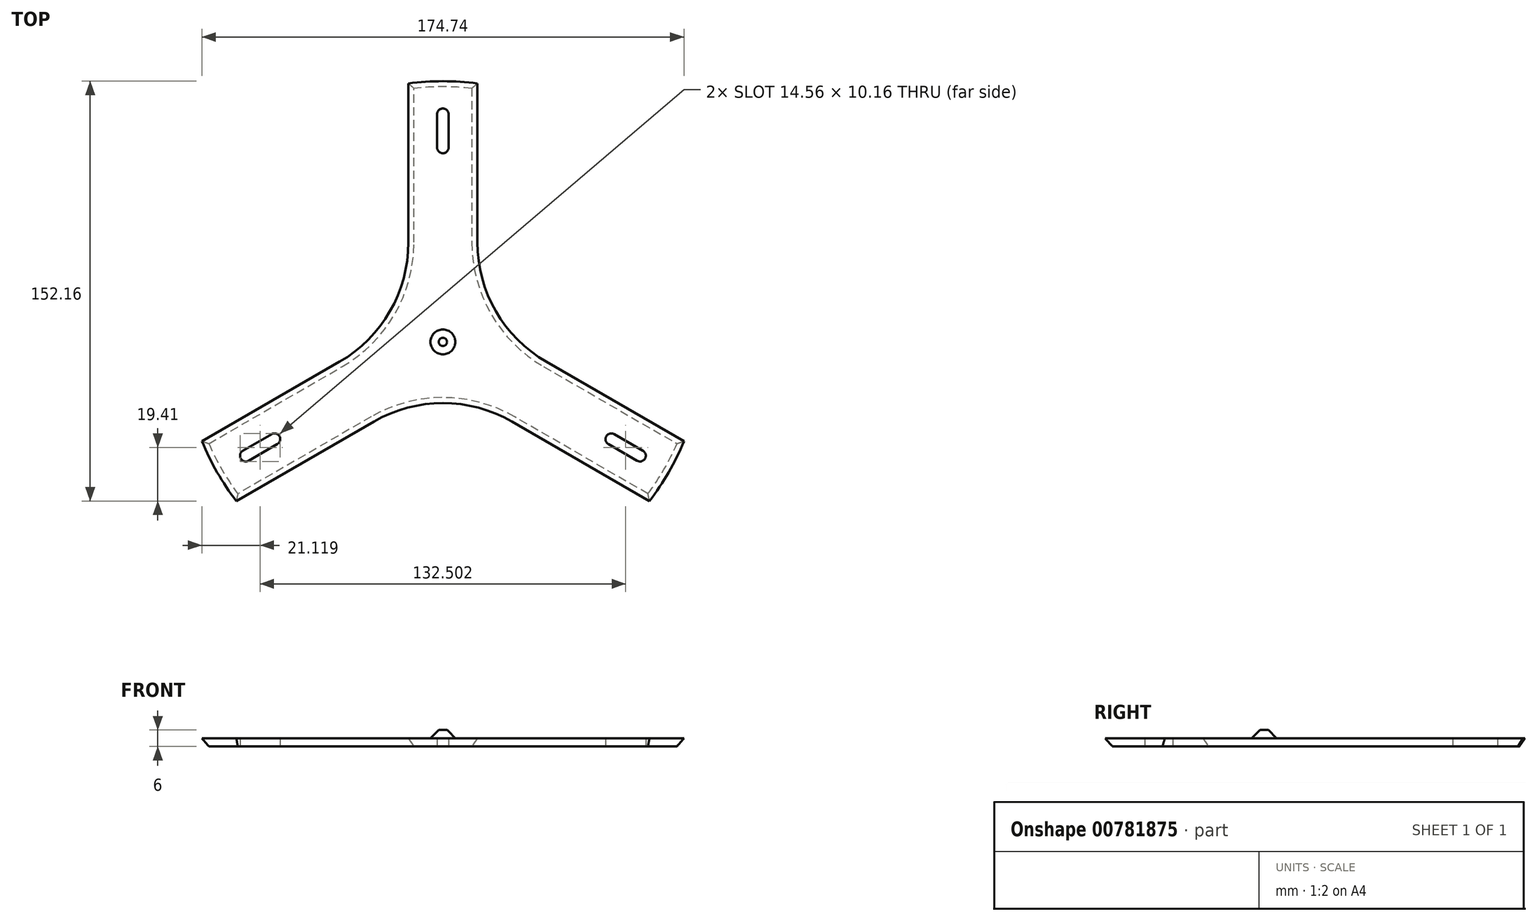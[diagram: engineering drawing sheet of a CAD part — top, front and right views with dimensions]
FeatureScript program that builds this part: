
annotation { "Feature Type Name" : "Feature", "Feature Type Description" : "" }
export const myFeature = defineFeature(function(context is Context, id is Id, definition is map)
    precondition{}
    {
        {
            var Q0;
            Q0=qCreatedBy(makeId("Top.planeOp"),FACE);
            var sketch = newSketch(context, id + "F0", { "sketchPlane" : qUnion([Q0])});
            skArc(sketch, "E0", {"start": v(12.5, 93.67) * mm, "mid": v(0, 94.5) * mm, "end": v(-12.5, 93.67) * mm});
            skCircle(sketch, "E1", {"center": v(0, 0) * mm, "radius": 76.5 * mm, "construction": true});
            skLineSegment(sketch, "E2", {"start": v(0, 0) * mm, "end": v(0, 94.5) * mm, "construction": true});
            skArc(sketch, "E3", {"start": v(-2.1, 70.5) * mm, "mid": v(0, 68.4) * mm, "end": v(2.1, 70.5) * mm});
            skArc(sketch, "E4", {"start": v(2.1, 82.5) * mm, "mid": v(0, 84.6) * mm, "end": v(-2.1, 82.5) * mm});
            skLineSegment(sketch, "E5", {"start": v(-2.1, 82.5) * mm, "end": v(-2.1, 70.5) * mm});
            skLineSegment(sketch, "E6", {"start": v(2.1, 82.5) * mm, "end": v(2.1, 70.5) * mm});
            skLineSegment(sketch, "E7.1.0", {"start": v(0, 0) * mm, "end": v(-81.84, 47.25) * mm, "construction": true});
            skLineSegment(sketch, "E7.2.0", {"start": v(0, 0) * mm, "end": v(-81.84, -47.25) * mm, "construction": true});
            skLineSegment(sketch, "E7.3.0", {"start": v(0, 0) * mm, "end": v(0, -94.5) * mm, "construction": true});
            skLineSegment(sketch, "E7.4.0", {"start": v(0, 0) * mm, "end": v(81.84, -47.25) * mm, "construction": true});
            skLineSegment(sketch, "E7.5.0", {"start": v(0, 0) * mm, "end": v(81.84, 47.25) * mm, "construction": true});
            skLineSegment(sketch, "E8", {"start": v(-12.5, 93.67) * mm, "end": v(-12.5, 7.22) * mm});
            skLineSegment(sketch, "E9.0.MirrorCS", {"start": v(12.5, 93.67) * mm, "end": v(12.5, 7.22) * mm});
            skArc(sketch, "E10.1.0", {"start": v(-87.37, -36) * mm, "mid": v(-81.84, -47.25) * mm, "end": v(-74.87, -57.66) * mm});
            skLineSegment(sketch, "E10.1.1", {"start": v(-87.37, -36) * mm, "end": v(-12.5, 7.22) * mm});
            skLineSegment(sketch, "E10.1.2", {"start": v(-74.87, -57.66) * mm, "end": v(0, -14.43) * mm});
            skLineSegment(sketch, "E10.1.3", {"start": v(-70.4, -43.07) * mm, "end": v(-60, -37.07) * mm});
            skLineSegment(sketch, "E10.1.4", {"start": v(-72.5, -39.43) * mm, "end": v(-62.1, -33.43) * mm});
            skArc(sketch, "E10.1.5", {"start": v(-72.5, -39.43) * mm, "mid": v(-73.27, -42.3) * mm, "end": v(-70.4, -43.07) * mm});
            skArc(sketch, "E10.1.6", {"start": v(-60, -37.07) * mm, "mid": v(-59.24, -34.2) * mm, "end": v(-62.1, -33.43) * mm});
            skArc(sketch, "E10.2.0", {"start": v(74.87, -57.66) * mm, "mid": v(81.84, -47.25) * mm, "end": v(87.37, -36) * mm});
            skLineSegment(sketch, "E10.2.1", {"start": v(74.87, -57.66) * mm, "end": v(0, -14.43) * mm});
            skLineSegment(sketch, "E10.2.2", {"start": v(87.37, -36) * mm, "end": v(12.5, 7.22) * mm});
            skLineSegment(sketch, "E10.2.3", {"start": v(72.5, -39.43) * mm, "end": v(62.1, -33.43) * mm});
            skLineSegment(sketch, "E10.2.4", {"start": v(70.4, -43.07) * mm, "end": v(60, -37.07) * mm});
            skArc(sketch, "E10.2.5", {"start": v(70.4, -43.07) * mm, "mid": v(73.27, -42.3) * mm, "end": v(72.5, -39.43) * mm});
            skArc(sketch, "E10.2.6", {"start": v(62.1, -33.43) * mm, "mid": v(59.24, -34.2) * mm, "end": v(60, -37.07) * mm});
            skSolve(sketch);
        }
        {
            var Q0;
            Q0=qSketchRegion(id+"F0",true);
            extrude(context, id + "F1", {"entities" : qUnion([Q0]), "depth" : 3 * mm});
        }
        {
            var Q0;
            Q0=makeQuery(id+"F1.opExtrude","CAP_FACE",FACE,{"disambiguationData":[OSD([sQuery(id+"F0.wireOp",EDGE,"E0"),sQuery(id+"F0.wireOp",EDGE,"E3"),sQuery(id+"F0.wireOp",EDGE,"E4"),sQuery(id+"F0.wireOp",EDGE,"E5"),sQuery(id+"F0.wireOp",EDGE,"E6"),sQuery(id+"F0.wireOp",EDGE,"E8"),sQuery(id+"F0.wireOp",EDGE,"E9.0.MirrorCS"),sQuery(id+"F0.wireOp",EDGE,"E10.1.0"),sQuery(id+"F0.wireOp",EDGE,"E10.1.1"),sQuery(id+"F0.wireOp",EDGE,"E10.1.2"),sQuery(id+"F0.wireOp",EDGE,"E10.1.3"),sQuery(id+"F0.wireOp",EDGE,"E10.1.4"),sQuery(id+"F0.wireOp",EDGE,"E10.1.5"),sQuery(id+"F0.wireOp",EDGE,"E10.1.6"),sQuery(id+"F0.wireOp",EDGE,"E10.2.0"),sQuery(id+"F0.wireOp",EDGE,"E10.2.1"),sQuery(id+"F0.wireOp",EDGE,"E10.2.2"),sQuery(id+"F0.wireOp",EDGE,"E10.2.3"),sQuery(id+"F0.wireOp",EDGE,"E10.2.4"),sQuery(id+"F0.wireOp",EDGE,"E10.2.5"),sQuery(id+"F0.wireOp",EDGE,"E10.2.6")])],"isStart":false});
            var sketch = newSketch(context, id + "F2", { "sketchPlane" : qUnion([Q0])});
            skCircle(sketch, "E11", {"center": v(0, 0) * mm, "radius": 4.5 * mm});
            skSolve(sketch);
        }
        {
            var Q0;
            Q0=qSketchRegion(id+"F2",true);
            extrude(context, id + "F3", {"entities" : qUnion([Q0]), "operationType" : NewBodyOperationType.ADD, "depth" : 3 * mm});
        }
        {
            var Q0;
            Q0=makeQuery(id+"F3.opExtrude","CAP_EDGE",EDGE,{"disambiguationData":[OSD([sQuery(id+"F2.wireOp",EDGE,"E11")])],"isStart":false});
            chamfer(context, id + "F4", {"entities" : qUnion([Q0]), "width" : 3 * mm, "tangentPropagation" : true});
        }
        {
            var Q0;
            Q0=makeQuery(id+"F1.opExtrude","CAP_EDGE",EDGE,{"disambiguationData":[OSD([sQuery(id+"F0.wireOp",EDGE,"E10.1.0")])],"isStart":true});
            var Q1;
            Q1=makeQuery(id+"F1.opExtrude","CAP_EDGE",EDGE,{"disambiguationData":[OSD([sQuery(id+"F0.wireOp",EDGE,"E10.2.0")])],"isStart":true});
            var Q2;
            Q2=makeQuery(id+"F1.opExtrude","CAP_EDGE",EDGE,{"disambiguationData":[OSD([sQuery(id+"F0.wireOp",EDGE,"E0")])],"isStart":true});
            chamfer(context, id + "F5", {"entities" : qUnion([Q0, Q1, Q2]), "chamferType" : ChamferType.TWO_OFFSETS, "width1" : 3 * mm, "oppositeDirection" : false, "width2" : 2 * mm, "tangentPropagation" : true});
        }
        {
            var Q0;
            Q0=makeQuery(id+"F1.opExtrude","SWEPT_EDGE",EDGE,{"disambiguationData":[OSD([sQuery(id+"F0.wireOp",EDGE,"E8"),sQuery(id+"F0.wireOp",EDGE,"E10.1.1")])]});
            var Q1;
            Q1=makeQuery(id+"F1.opExtrude","SWEPT_EDGE",EDGE,{"disambiguationData":[OSD([sQuery(id+"F0.wireOp",EDGE,"E10.1.2"),sQuery(id+"F0.wireOp",EDGE,"E10.2.1")])]});
            var Q2;
            Q2=makeQuery(id+"F1.opExtrude","SWEPT_EDGE",EDGE,{"disambiguationData":[OSD([sQuery(id+"F0.wireOp",EDGE,"E9.0.MirrorCS"),sQuery(id+"F0.wireOp",EDGE,"E10.2.2")])]});
            fillet(context, id + "F6", {"entities" : qUnion([Q0, Q1, Q2]), "radius" : 50 * mm, "tangentPropagation" : true, "allowEdgeOverflow" : false});
        }
        {
            var Q0;
            Q0=makeQuery(id+"F1.opExtrude","CAP_EDGE",EDGE,{"disambiguationData":[OSD([sQuery(id+"F0.wireOp",EDGE,"E10.2.1")])],"isStart":true});
            var Q1;
            Q1=makeQuery(id+"F1.opExtrude","CAP_EDGE",EDGE,{"disambiguationData":[OSD([sQuery(id+"F0.wireOp",EDGE,"E10.2.2")])],"isStart":true});
            var Q2;
            {var subQ0=sQuery(id+"F0.wireOp",EDGE,"E8");var subQ1=sQuery(id+"F0.wireOp",EDGE,"E10.1.1");Q2=makeQuery(id+"F6.opFillet","BLEND_EDGE",EDGE,{"blendedFrom":[makeQuery(id+"F1.opExtrude","SWEPT_EDGE",EDGE,{"disambiguationData":[OSD([subQ0,subQ1])]}),makeQuery(id+"F1.opExtrude","CAP_FACE",FACE,{"disambiguationData":[OSD([sQuery(id+"F0.wireOp",EDGE,"E0"),sQuery(id+"F0.wireOp",EDGE,"E3"),sQuery(id+"F0.wireOp",EDGE,"E4"),sQuery(id+"F0.wireOp",EDGE,"E5"),sQuery(id+"F0.wireOp",EDGE,"E6"),subQ0,sQuery(id+"F0.wireOp",EDGE,"E9.0.MirrorCS"),sQuery(id+"F0.wireOp",EDGE,"E10.1.0"),subQ1,sQuery(id+"F0.wireOp",EDGE,"E10.1.2"),sQuery(id+"F0.wireOp",EDGE,"E10.1.3"),sQuery(id+"F0.wireOp",EDGE,"E10.1.4"),sQuery(id+"F0.wireOp",EDGE,"E10.1.5"),sQuery(id+"F0.wireOp",EDGE,"E10.1.6"),sQuery(id+"F0.wireOp",EDGE,"E10.2.0"),sQuery(id+"F0.wireOp",EDGE,"E10.2.1"),sQuery(id+"F0.wireOp",EDGE,"E10.2.2"),sQuery(id+"F0.wireOp",EDGE,"E10.2.3"),sQuery(id+"F0.wireOp",EDGE,"E10.2.4"),sQuery(id+"F0.wireOp",EDGE,"E10.2.5"),sQuery(id+"F0.wireOp",EDGE,"E10.2.6")])],"isStart":true})],"blendedInto":[makeQuery(id+"F1.opExtrude","CAP_FACE",FACE,{"disambiguationData":[OSD([sQuery(id+"F0.wireOp",EDGE,"E0"),sQuery(id+"F0.wireOp",EDGE,"E3"),sQuery(id+"F0.wireOp",EDGE,"E4"),sQuery(id+"F0.wireOp",EDGE,"E5"),sQuery(id+"F0.wireOp",EDGE,"E6"),subQ0,sQuery(id+"F0.wireOp",EDGE,"E9.0.MirrorCS"),sQuery(id+"F0.wireOp",EDGE,"E10.1.0"),subQ1,sQuery(id+"F0.wireOp",EDGE,"E10.1.2"),sQuery(id+"F0.wireOp",EDGE,"E10.1.3"),sQuery(id+"F0.wireOp",EDGE,"E10.1.4"),sQuery(id+"F0.wireOp",EDGE,"E10.1.5"),sQuery(id+"F0.wireOp",EDGE,"E10.1.6"),sQuery(id+"F0.wireOp",EDGE,"E10.2.0"),sQuery(id+"F0.wireOp",EDGE,"E10.2.1"),sQuery(id+"F0.wireOp",EDGE,"E10.2.2"),sQuery(id+"F0.wireOp",EDGE,"E10.2.3"),sQuery(id+"F0.wireOp",EDGE,"E10.2.4"),sQuery(id+"F0.wireOp",EDGE,"E10.2.5"),sQuery(id+"F0.wireOp",EDGE,"E10.2.6")])],"isStart":true})]});}
            chamfer(context, id + "F7", {"entities" : qUnion([Q0, Q1, Q2]), "chamferType" : ChamferType.TWO_OFFSETS, "width1" : 2 * mm, "oppositeDirection" : false, "width2" : 3 * mm, "tangentPropagation" : true});
        }
    });
